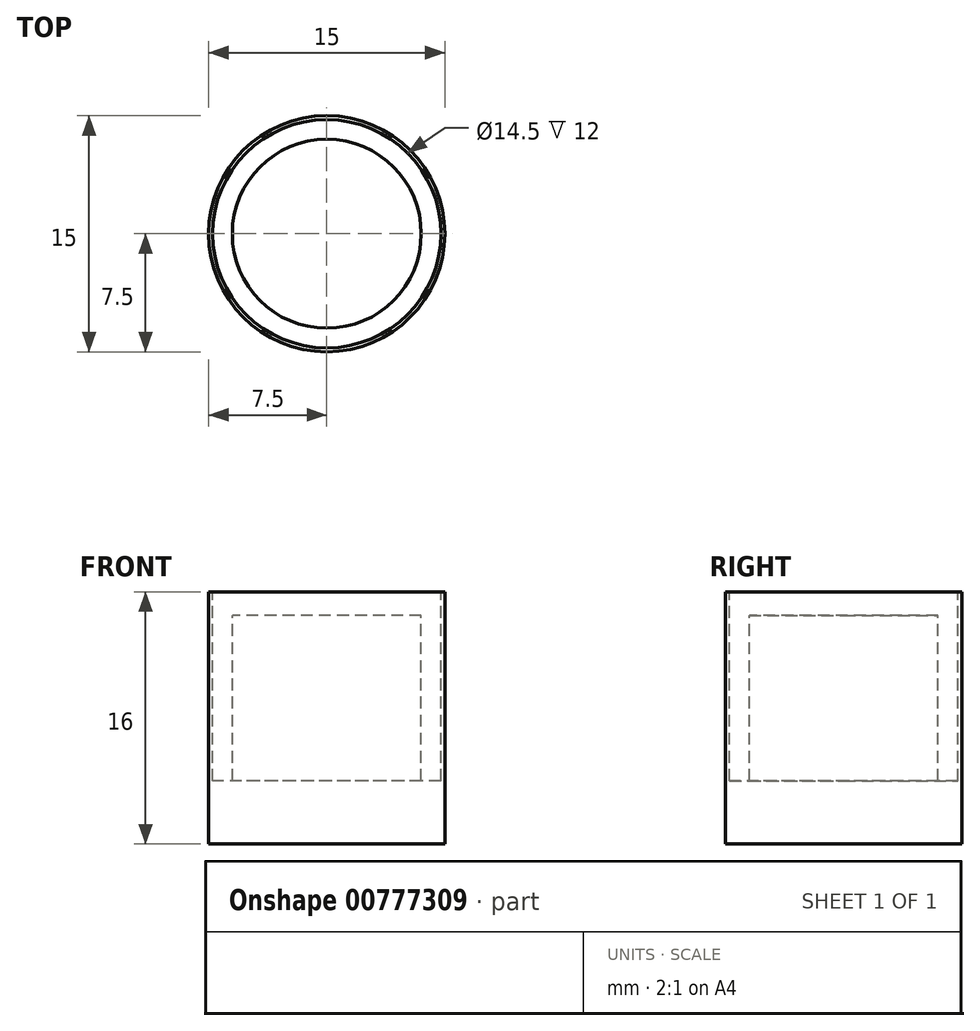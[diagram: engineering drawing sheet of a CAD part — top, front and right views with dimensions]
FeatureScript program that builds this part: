
annotation { "Feature Type Name" : "Feature", "Feature Type Description" : "" }
export const myFeature = defineFeature(function(context is Context, id is Id, definition is map)
    precondition{}
    {
        {
            var Q0;
            Q0=qCreatedBy(makeId("Top.planeOp"),FACE);
            var sketch = newSketch(context, id + "F0", { "sketchPlane" : qUnion([Q0])});
            skCircle(sketch, "E0", {"center": v(0, 0) * mm, "radius": 7.5 * mm});
            skCircle(sketch, "E1", {"center": v(0, 0) * mm, "radius": 6 * mm});
            skCircle(sketch, "E2", {"center": v(0, 0) * mm, "radius": 7.25 * mm});
            skSolve(sketch);
        }
        {
            var Q0;
            Q0=makeQuery(id+"F0.imprint","IMPRINT",FACE,{"disambiguationData":[TD([[makeQuery(id+"F0.imprint","IMPRINT",EDGE,{"derivedFrom":sQuery(id+"F0.wireOp",EDGE,"E0")}),1.0]])]});
            var Q1;
            Q1=makeQuery(id+"F0.imprint","IMPRINT",FACE,{"disambiguationData":[TD([[makeQuery(id+"F0.imprint","IMPRINT",EDGE,{"derivedFrom":sQuery(id+"F0.wireOp",EDGE,"E1")}),1.0]])]});
            var Q2;
            Q2=makeQuery(id+"F0.imprint","IMPRINT",FACE,{"disambiguationData":[TD([[makeQuery(id+"F0.imprint","IMPRINT",EDGE,{"derivedFrom":sQuery(id+"F0.wireOp",EDGE,"E1")}),-1.0]])]});
            extrude(context, id + "F1", {"entities" : qUnion([Q0, Q1, Q2]), "oppositeDirection" : true, "depth" : 16 * mm, "offsetDistance" : 25 * mm});
        }
        {
            var Q0;
            Q0=makeQuery(id+"F0.imprint","IMPRINT",FACE,{"disambiguationData":[TD([[makeQuery(id+"F0.imprint","IMPRINT",EDGE,{"derivedFrom":sQuery(id+"F0.wireOp",EDGE,"E1")}),-1.0]])]});
            extrude(context, id + "F2", {"entities" : qUnion([Q0]), "operationType" : NewBodyOperationType.REMOVE, "oppositeDirection" : true, "depth" : 12 * mm, "offsetDistance" : 25 * mm});
        }
        {
            var Q0;
            Q0=makeQuery(id+"F0.imprint","IMPRINT",FACE,{"disambiguationData":[TD([[makeQuery(id+"F0.imprint","IMPRINT",EDGE,{"derivedFrom":sQuery(id+"F0.wireOp",EDGE,"E1")}),1.0]])]});
            extrude(context, id + "F3", {"entities" : qUnion([Q0]), "operationType" : NewBodyOperationType.REMOVE, "oppositeDirection" : true, "depth" : 1.5 * mm, "offsetDistance" : 25 * mm});
        }
    });
